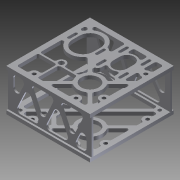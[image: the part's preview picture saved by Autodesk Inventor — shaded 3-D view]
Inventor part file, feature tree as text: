
AUTODESK INVENTOR PART (.ipt)
format: ipt  version: 2012 (Build 160160000, 160)  size: 920,064 bytes
history: native  units: in
note: dims shown in document units (in); Inventor stores cm internally (conversion verified against a paired STEP export)
features: thread x8, extrude x7, sketch x5, fillet x3, projected_geometry x1
ambient origin geometry x8: Origin, YZ Plane, XZ Plane, XY Plane, X Axis, Y Axis, Z Axis, Center Point
bodies: Solid1 (feature_tree)
feature tree (24):
  extrude  "Extrusion1"  Depth=0.1875in
  sketch  "Sketch2"  dims[d4=0.25in d5=0.25in d6=6.0in d7=0.0in]
  extrude  "Extrusion2"  Depth=6.0in TaperAngle=0.0deg
  extrude  "Extrusion3"  Depth=1.25in
  extrude  "Extrusion4"  Depth=1.5in
  fillet  "Fillet2"  Radius=0.375in
  sketch  "Sketch6"  dims[d20=0.25in d21=0.125in d22=0.25in d24=0.25in d25=0.125in d27=0.125in d32=0.25in d33=0.0in d35=0.375in d36=0.375in d37=0.375in d38=0.375in d39=0.1719in d40=0.3438in d41=0.3438in d42=0.3438in d43=0.3438in d44=0.125in d46=0.125in d49=0.125in d50=0.125in d51=0.125in d52=0.125in d53=0.125in d54=0.125in d55=0.125in d56=0.125in d57=0.25in d58=0.0in d60=0.3798in d61=0.287in d62=0.287in d63=0.287in d64=0.125in d65=0.125in d66=0.125in d67=0.125in d68=0.125in d69=0.125in d70=0.125in d71=0.125in d72=0.125in d73=0.125in d74=0.375in d76=0.25in d77=0.375in d78=0.375in d79=0.25in d80=0.0in d81=0.25in d88=0.125in d89=1.25in d90=1.5in d91=0.75in d92=0.5in d94=0.2in d96=0.9in d97=1.0in d98=0.5in d99=0.5in d101=2.0in d102=0.2in d103=0.8in d104=0.8in d105=0.7874in d107=1.6in d108=0.7874in d110=1.6in d114=1.0in d115=1.0in d116=1.5in d117=1.0in d119=0.2in d122=4.5in d123=1.3125in d124=0.366in d126=2.3in d127=0.25in d128=0.0in d129=0.375in d131=4.5in d132=0.125in d153=0.25in d154=0.125in d156=0.375in d157=0.375in d160=0.25in d161=0.125in d162=0.25in d163=0.125in d165=0.875in d166=0.125in d168=0.3125in d169=0.125in d170=0.125in d171=1.0in d172=0.25in d177=0.125in d178=0.6in d179=0.25in d180=0.0in d181=0.125in d183=0.25in d185=0.25in d186=0.125in d188=1.5625in d190=1.3125in d191=0.366in d193=0.25in d194=0.125in d197=1.0in d198=1.176in d199=0.1in d200=0.0in d201=0.0625in d203=0.25in d204=0.125in d205=0.0625in d207=2.1875in d208=1.9688in d211=0.125in d212=0.3in d213=0.5in d214=0.25in d215=0.3125in d220=0.5in d221=1.5in d222=0.25in d224=0.1875in d225=2.3in d226=0.35in d227=0.25in d228=1.5in d229=1.5in d230=0.5821in d231=0.25in d232=1.5in d233=0.125in d234=0.25in d235=2.0in d236=0.25in d237=1.5in d238=0.3125in d239=0.7874in d241=3.0in d242=0.3937in d244=1.0in d246=1.5in d247=0.7874in d249=3.0in d250=0.3937in d252=1.0in d254=0.5in d255=0.25in d256=0.3125in d257=0.25in d258=0.5in d259=0.3125in d260=0.25in d262=0.625in d264=6.0in d267=0.25in d269=3.0in d270=6.0in d272=0.25in d273=0.125in d274=0.125in d275=0.1435in d276=2.0in d277=1.0in d278=0.0in d279=1.0in d280=0.0in d281=1.0in d282=0.0in d283=1.0in d284=0.0in d285=1.0in d286=0.0in d287=1.0in d288=0.0in d289=1.0in d290=0.0in d291=1.0in d292=0.0in d293=0.125in d294=0.125in d295=0.125in d296=0.625in]
  fillet  "Fillet3"  Radius=0.875in
  extrude  "Extrusion5"  Depth=0.125in
  extrude  "Extrusion6"  Depth=0.25in
  fillet  "Fillet4"  Radius=0.25in
  extrude  "Extrusion7"  Depth=0.125in
  thread  "Thread1"  [1 undecoded]
  thread  "Thread2"  [1 undecoded]
  thread  "Thread3"  [1 undecoded]
  thread  "Thread4"  [1 undecoded]
  thread  "Thread5"  [1 undecoded]
  thread  "Thread6"  [1 undecoded]
  thread  "Thread7"  [1 undecoded]
  thread  "Thread8"  [1 undecoded]
  sketch  "Sketch1"  dims[d1=3.0in d2=0.1875in d3=0.25in]
  sketch  "Sketch4"  dims[d11=1.9688in d13=1.25in]
  sketch  "Sketch5"  dims[d15=2.625in d16=1.5in d18=0.375in d19=0.875in]
  projected_geometry  "Projected Loop1"
note: 8 required parameter values undecoded (feature->parameter linkage not recoverable at this tier; creation-order binding heuristic only, values carry confidence <= 0.55)
